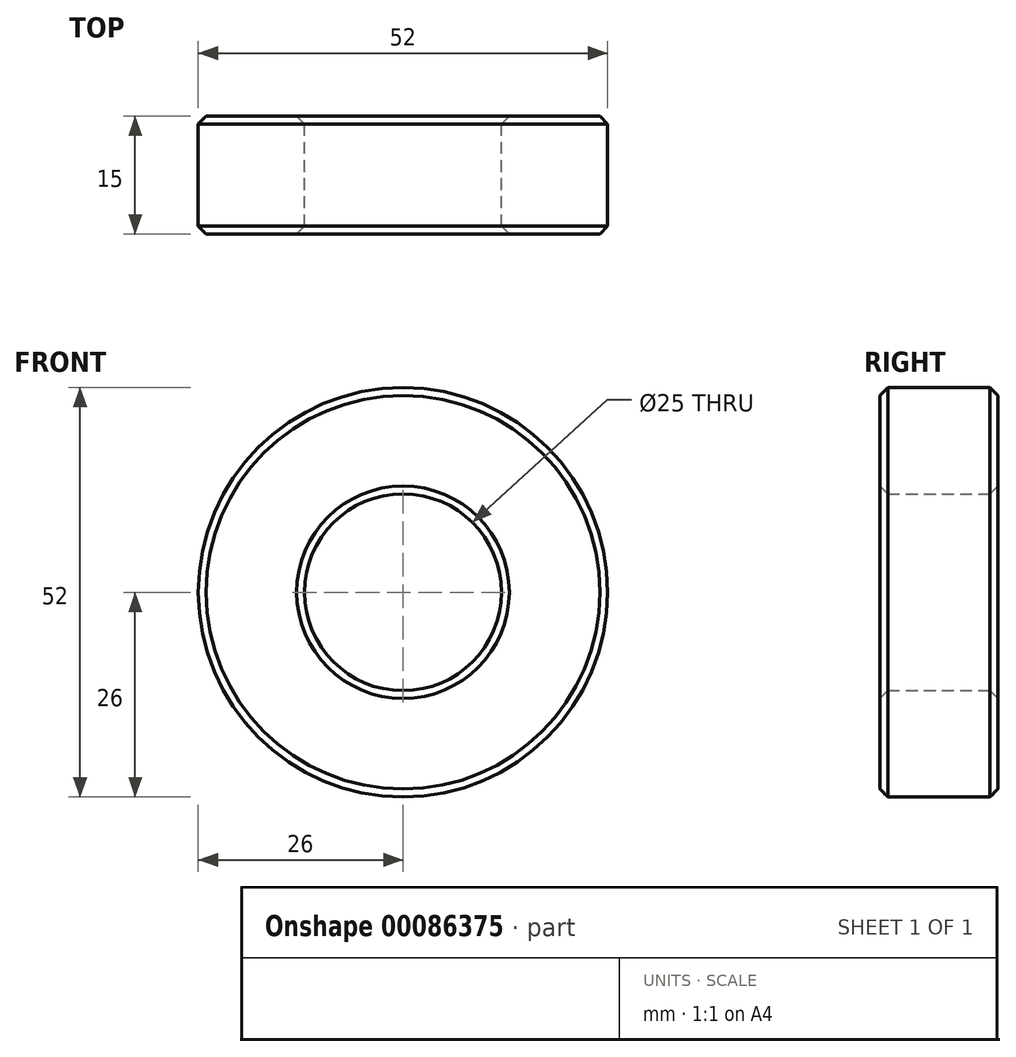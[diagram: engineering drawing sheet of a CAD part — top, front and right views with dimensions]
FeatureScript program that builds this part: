
annotation { "Feature Type Name" : "Feature", "Feature Type Description" : "" }
export const myFeature = defineFeature(function(context is Context, id is Id, definition is map)
    precondition{}
    {
        {
            var Q0;
            Q0=qCreatedBy(makeId("Front.planeOp"),FACE);
            var sketch = newSketch(context, id + "F0", { "sketchPlane" : qUnion([Q0])});
            skCircle(sketch, "E0", {"center": v(0, 0) * mm, "radius": 26 * mm});
            skCircle(sketch, "E1", {"center": v(0, 0) * mm, "radius": 12.5 * mm});
            skSolve(sketch);
        }
        {
            var Q0;
            Q0 = qSketchRegion(id + "F0", true);
            extrude(context, id + "F1", {"entities" : qUnion([Q0]), "depth" : 15 * mm, "offsetDistance" : 25 * mm});
        }
        {
            var Q0;
            Q0=makeQuery(id+"F1.opExtrude","CAP_FACE",FACE,{"disambiguationData":[OSD([sQuery(id+"F0.wireOp",EDGE,"E0"),sQuery(id+"F0.wireOp",EDGE,"E1")])],"isStart":false});
            var Q1;
            Q1=makeQuery(id+"F1.opExtrude","CAP_FACE",FACE,{"disambiguationData":[OSD([sQuery(id+"F0.wireOp",EDGE,"E0"),sQuery(id+"F0.wireOp",EDGE,"E1")])],"isStart":true});
            chamfer(context, id + "F2", {"entities" : qUnion([Q0, Q1]), "width" : 1 * mm, "tangentPropagation" : true});
        }
    });
